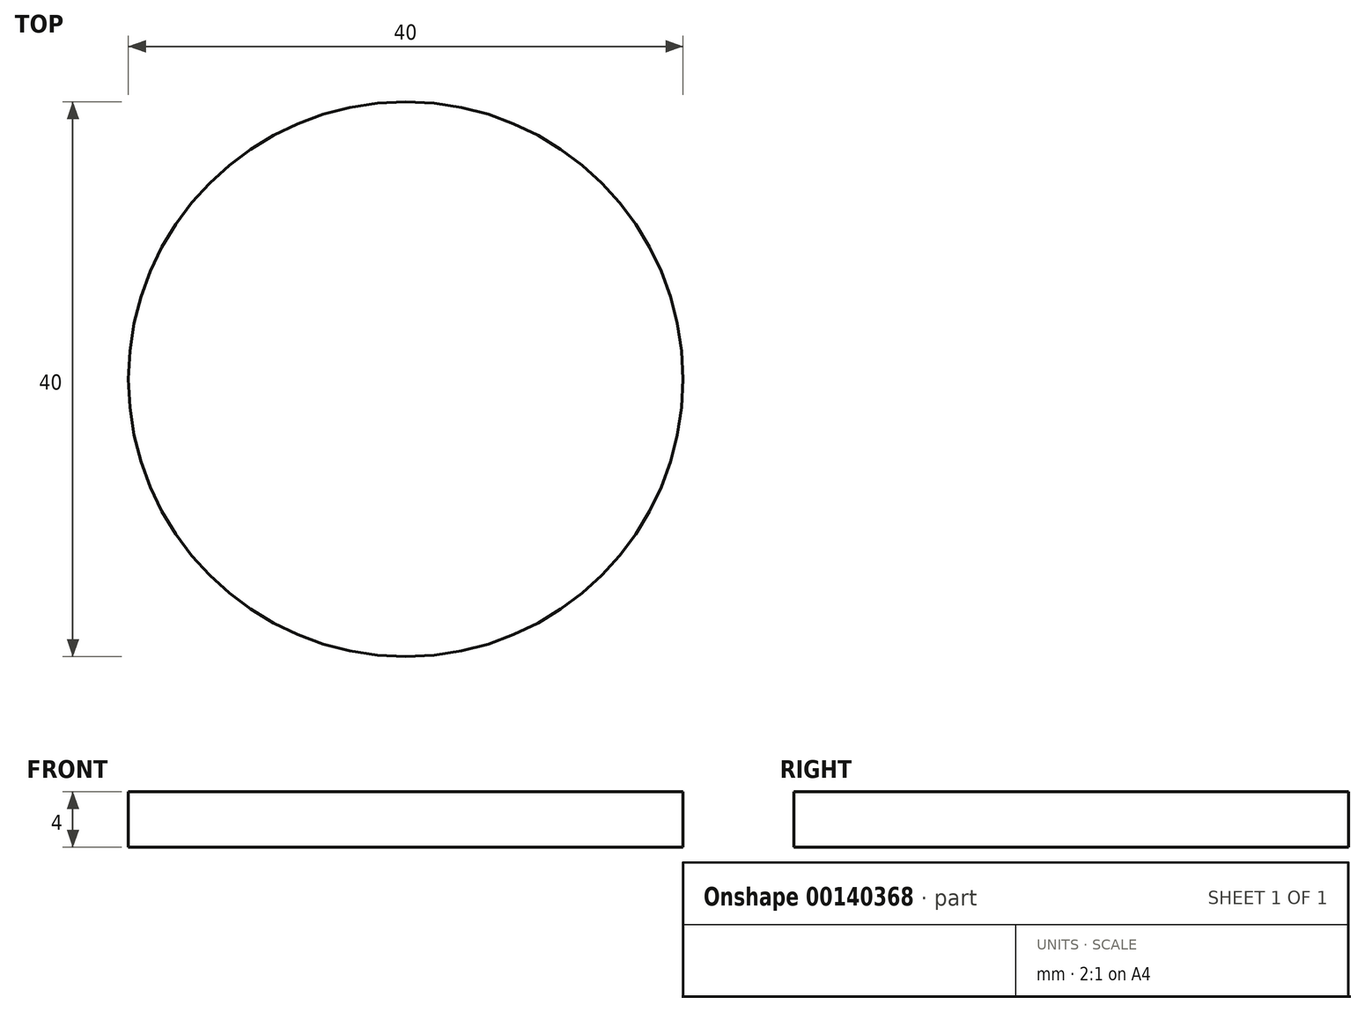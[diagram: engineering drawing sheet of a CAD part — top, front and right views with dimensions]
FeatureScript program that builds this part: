
annotation { "Feature Type Name" : "Feature", "Feature Type Description" : "" }
export const myFeature = defineFeature(function(context is Context, id is Id, definition is map)
    precondition{}
    {
        {
            var Q0;
            Q0=qCreatedBy(makeId("Top.planeOp"),FACE);
            var sketch = newSketch(context, id + "F0", { "sketchPlane" : qUnion([Q0])});
            skLineSegment(sketch, "E0", {"start": v(27.85, -21.2) * mm, "end": v(27.85, -21.2) * mm});
            skCircle(sketch, "E1", {"center": v(0, 0) * mm, "radius": 7.5 * mm});
            skLineSegment(sketch, "E2", {"start": v(0, 0) * mm, "end": v(0, -35) * mm});
            skLineSegment(sketch, "E3", {"start": v(0, -35) * mm, "end": v(0, -145) * mm});
            skCircle(sketch, "E4", {"center": v(0, -145) * mm, "radius": 20 * mm});
            skFitSpline(sketch, "E5", {"points": [v(20, -145) * mm, v(20.1, -76.6) * mm, v(27.85, -21.2) * mm, v(27.85, -21.2) * mm], "startDerivative": vector(-9.9, 119.95) * mm, "endDerivative": vector(5.01, -7.3) * mm});
            skPoint(sketch, "E6.newPointB", {"position": v(-20, -145) * mm});
            skArc(sketch, "E6.filletArc", {"start": v(-27.36, -25.35) * mm, "mid": v(-28.32, -21.57) * mm, "end": v(-30, -18.04) * mm});
            skArc(sketch, "E7.MirrorCS", {"start": v(27.36, -25.35) * mm, "mid": v(28.32, -21.57) * mm, "end": v(30, -18.04) * mm});
            skFitSpline(sketch, "E8.MirrorCS", {"points": [v(-20, -145) * mm, v(-20.1, -76.6) * mm, v(-27.85, -21.2) * mm, v(-27.85, -21.2) * mm], "startDerivative": vector(9.9, 119.95) * mm, "endDerivative": vector(-5.01, -7.3) * mm});
            skArc(sketch, "E9.trimOffspring", {"start": v(30, -18.04) * mm, "mid": v(0, 35) * mm, "end": v(-30, -18.04) * mm});
            skSolve(sketch);
        }
        {
            var Q0;
            Q0=makeQuery(id+"F0.imprint","IMPRINT",FACE,{"disambiguationData":[TD([[makeQuery(id+"F0.imprint","IMPRINT",EDGE,{"derivedFrom":sQuery(id+"F0.wireOp",EDGE,"E1")}),-1.0]])]});
            var Q1;
            {var subQ1=sQuery(id+"F0.wireOp",EDGE,"E4");var subQ6=makeQuery(id+"F0.imprint","INTERSECT",VERTEX,{"derivedFrom":[sQuery(id+"F0.wireOp",EDGE,"E3"),subQ1]});Q1=makeQuery(id+"F0.imprint","IMPRINT",FACE,{"disambiguationData":[TD([[makeQuery(id+"F0.imprint","IMPRINT",EDGE,{"disambiguationData":[TD([[subQ6,1.0]])],"derivedFrom":subQ1}),1.0]])]});}
            var Q2;
            {var subQ0=sQuery(id+"F0.wireOp",EDGE,"E3");var subQ1=sQuery(id+"F0.wireOp",EDGE,"E0");var subQ2=makeQuery(id+"F0.imprint","INTERSECT",VERTEX,{"derivedFrom":[subQ1,subQ0]});Q2=makeQuery(id+"F0.imprint","IMPRINT",FACE,{"disambiguationData":[TD([[makeQuery(id+"F0.imprint","IMPRINT",EDGE,{"disambiguationData":[TD([[subQ2,1.0]])],"derivedFrom":subQ1}),-1.0]])]});}
            var Q3;
            {var subQ0=sQuery(id+"F0.wireOp",EDGE,"E3");var subQ1=sQuery(id+"F0.wireOp",EDGE,"E0");var subQ2=makeQuery(id+"F0.imprint","INTERSECT",VERTEX,{"derivedFrom":[subQ1,subQ0]});Q3=makeQuery(id+"F0.imprint","IMPRINT",FACE,{"disambiguationData":[TD([[makeQuery(id+"F0.imprint","IMPRINT",EDGE,{"disambiguationData":[TD([[subQ2,-1.0]])],"derivedFrom":subQ1}),-1.0]])]});}
            extrude(context, id + "F1", {"entities" : qUnion([Q0, Q1, Q2, Q3]), "depth" : 4 * mm});
        }
    });
